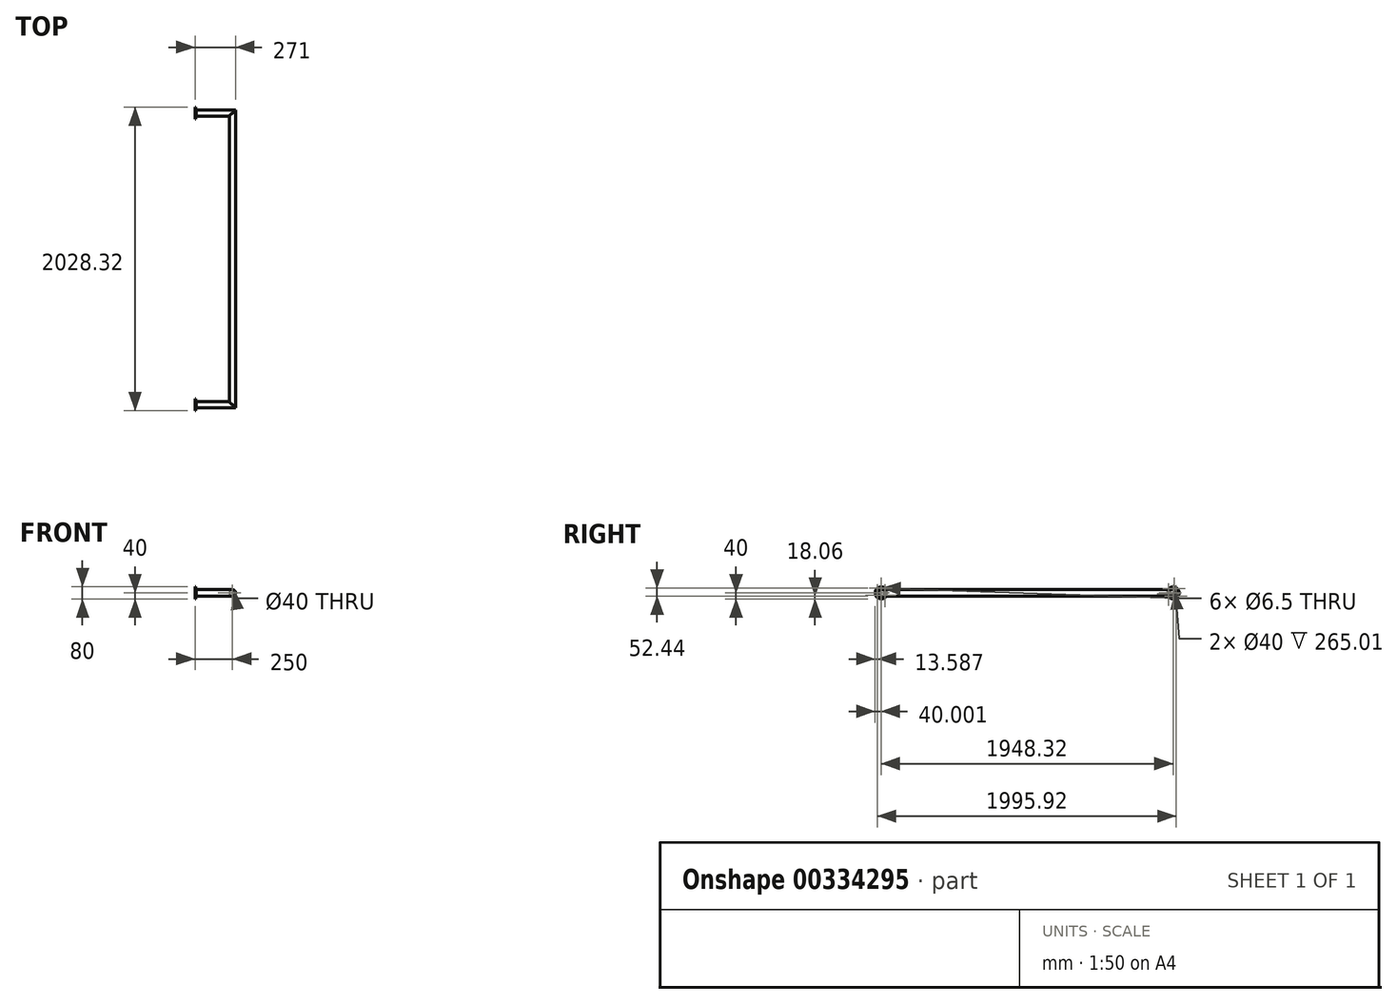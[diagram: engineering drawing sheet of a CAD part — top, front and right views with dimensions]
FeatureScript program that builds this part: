
annotation { "Feature Type Name" : "Feature", "Feature Type Description" : "" }
export const myFeature = defineFeature(function(context is Context, id is Id, definition is map)
    precondition{}
    {
        {
            var Q0;
            Q0=qCreatedBy(makeId("Right.planeOp"),FACE);
            var sketch = newSketch(context, id + "F0", { "sketchPlane" : qUnion([Q0])});
            skCircle(sketch, "E0", {"center": v(0, 0) * mm, "radius": 20 * mm});
            skCircle(sketch, "E1", {"center": v(0, 0) * mm, "radius": 21 * mm});
            skSolve(sketch);
        }
        {
            var Q0;
            Q0=qCreatedBy(makeId("Top.planeOp"),FACE);
            var sketch = newSketch(context, id + "F1", { "sketchPlane" : qUnion([Q0])});
            skLineSegment(sketch, "E2", {"start": v(0, 0) * mm, "end": v(250, 0) * mm});
            skLineSegment(sketch, "E3", {"start": v(250, 0) * mm, "end": v(250, -1948.32) * mm});
            skLineSegment(sketch, "E4", {"start": v(250, -1948.32) * mm, "end": v(0, -1948.32) * mm});
            skSolve(sketch);
        }
        {
            var Q0;
            Q0=makeQuery(id+"F0.imprint","IMPRINT",FACE,{"disambiguationData":[TD([[makeQuery(id+"F0.imprint","IMPRINT",EDGE,{"derivedFrom":sQuery(id+"F0.wireOp",EDGE,"E0")}),-1.0]])]});
            var Q1;
            Q1=sQuery(id+"F1.wireOp",EDGE,"E2");
            var Q2;
            Q2=sQuery(id+"F1.wireOp",EDGE,"E3");
            var Q3;
            Q3=sQuery(id+"F1.wireOp",EDGE,"E4");
            sweep(context, id + "F2", {"profiles" : qUnion([Q0]), "path" : qUnion([Q1, Q2, Q3])});
        }
        {
            var Q0;
            Q0=makeQuery(id+"F2.opSweep","CAP_FACE",FACE,{"disambiguationData":[OSD([sQuery(id+"F0.wireOp",EDGE,"E0"),sQuery(id+"F0.wireOp",EDGE,"E1"),sQuery(id+"F1.wireOp",VERTEX,"E4.end")])],"isStart":false});
            var sketch = newSketch(context, id + "F3", { "sketchPlane" : qUnion([Q0])});
            skCircle(sketch, "E5", {"center": v(1948.32, 0) * mm, "radius": 40 * mm});
            skLineSegment(sketch, "E6", {"start": v(1948.32, 40) * mm, "end": v(1948.32, -40) * mm, "construction": true});
            skPoint(sketch, "E7", {"position": v(1948.32, 21) * mm});
            skPoint(sketch, "E8", {"position": v(1948.32, -21) * mm});
            skLineSegment(sketch, "E9", {"start": v(2096.44, 30.5) * mm, "end": v(2107.58, 30.5) * mm, "construction": true});
            skLineSegment(sketch, "E10", {"start": v(2092.64, -30.5) * mm, "end": v(2107.79, -30.5) * mm, "construction": true});
            skPoint(sketch, "E11", {"position": v(1948.32, 30.5) * mm});
            skPoint(sketch, "E12", {"position": v(1948.32, -30.5) * mm});
            skCircle(sketch, "E13", {"center": v(1948.32, -30.5) * mm, "radius": 3.25 * mm, "construction": true});
            skCircle(sketch, "E14", {"center": v(1948.32, 30.5) * mm, "radius": 3.25 * mm});
            skCircle(sketch, "E15", {"center": v(0, 0) * mm, "radius": 40 * mm});
            skLineSegment(sketch, "E16", {"start": v(0, 40) * mm, "end": v(0, -40) * mm, "construction": true});
            skLineSegment(sketch, "E17", {"start": v(-15.2, 53.03) * mm, "end": v(15.2, -53.03) * mm, "construction": true});
            skPoint(sketch, "E18", {"position": v(-11.03, 38.45) * mm});
            skPoint(sketch, "E19", {"position": v(-3.3, 53.66) * mm});
            skPoint(sketch, "E20", {"position": v(-5.79, 20.19) * mm});
            skLineSegment(sketch, "E21", {"start": v(-8.4, 29.32) * mm, "end": v(-16.49, 27) * mm, "construction": true});
            skPoint(sketch, "E22", {"position": v(11.03, -38.45) * mm});
            skPoint(sketch, "E23", {"position": v(5.79, -20.19) * mm});
            skLineSegment(sketch, "E24", {"start": v(8.4, -29.32) * mm, "end": v(19.04, -26.27) * mm, "construction": true});
            skCircle(sketch, "E25", {"center": v(8.4, -29.32) * mm, "radius": 3.25 * mm, "construction": true});
            skCircle(sketch, "E26", {"center": v(-8.4, 29.32) * mm, "radius": 3.25 * mm});
            skCircle(sketch, "E27.1.0", {"center": v(-21.19, -21.94) * mm, "radius": 3.25 * mm});
            skCircle(sketch, "E27.2.0", {"center": v(29.6, -7.38) * mm, "radius": 3.25 * mm});
            skCircle(sketch, "E28.1.1", {"center": v(1921.9, -15.25) * mm, "radius": 3.25 * mm});
            skCircle(sketch, "E28.2.1", {"center": v(1974.73, -15.25) * mm, "radius": 3.25 * mm});
            skCircle(sketch, "E29", {"center": v(0, 0) * mm, "radius": 30.5 * mm, "construction": true});
            skLineSegment(sketch, "E30", {"start": v(0, 0) * mm, "end": v(29.6, -7.38) * mm, "construction": true});
            skLineSegment(sketch, "E31", {"start": v(0, 0) * mm, "end": v(-21.19, -21.94) * mm, "construction": true});
            skSolve(sketch);
        }
        {
            var Q0;
            Q0=qSketchRegion(id+"F3",true);
            extrude(context, id + "F4", {"entities" : qUnion([Q0]), "operationType" : NewBodyOperationType.ADD, "oppositeDirection" : true, "depth" : 5 * mm});
        }
        {
            var Q0;
            Q0=makeQuery(id+"F4.opExtrude","CAP_EDGE",EDGE,{"disambiguationData":[OSD([sQuery(id+"F3.wireOp",EDGE,"E26")])],"isStart":false});
            var Q1;
            Q1=makeQuery(id+"F4.opExtrude","CAP_EDGE",EDGE,{"disambiguationData":[OSD([sQuery(id+"F3.wireOp",EDGE,"E27.2.0")])],"isStart":false});
            var Q2;
            Q2=makeQuery(id+"F4.opExtrude","CAP_EDGE",EDGE,{"disambiguationData":[OSD([sQuery(id+"F3.wireOp",EDGE,"E27.1.0")])],"isStart":false});
            var Q3;
            Q3=makeQuery(id+"F4.opExtrude","CAP_EDGE",EDGE,{"disambiguationData":[OSD([sQuery(id+"F3.wireOp",EDGE,"E14")])],"isStart":false});
            var Q4;
            Q4=makeQuery(id+"F4.opExtrude","CAP_EDGE",EDGE,{"disambiguationData":[OSD([sQuery(id+"F3.wireOp",EDGE,"E28.2.1")])],"isStart":false});
            var Q5;
            Q5=makeQuery(id+"F4.opExtrude","CAP_EDGE",EDGE,{"disambiguationData":[OSD([sQuery(id+"F3.wireOp",EDGE,"E28.1.1")])],"isStart":false});
            chamfer(context, id + "F5", {"entities" : qUnion([Q0, Q1, Q2, Q3, Q4, Q5]), "width" : 2 * mm, "tangentPropagation" : true});
        }
        {
            var Q0;
            Q0=makeQuery(id+"F4.boolean.opBoolean","INTERSECT",EDGE,{"derivedFrom":[makeQuery(id+"F2.opSweep","SWEPT_FACE",FACE,{"disambiguationData":[OSD([sQuery(id+"F0.wireOp",EDGE,"E1"),sQuery(id+"F1.wireOp",EDGE,"E2")])]}),makeQuery(id+"F4.opExtrude","CAP_FACE",FACE,{"disambiguationData":[OSD([sQuery(id+"F3.wireOp",EDGE,"E15"),sQuery(id+"F3.wireOp",EDGE,"E26"),sQuery(id+"F3.wireOp",EDGE,"E27.1.0"),sQuery(id+"F3.wireOp",EDGE,"E27.2.0")])],"isStart":false})]});
            var Q1;
            Q1=makeQuery(id+"F4.boolean.opBoolean","INTERSECT",EDGE,{"derivedFrom":[makeQuery(id+"F2.opSweep","SWEPT_FACE",FACE,{"disambiguationData":[OSD([sQuery(id+"F0.wireOp",EDGE,"E1"),sQuery(id+"F1.wireOp",EDGE,"E4")])]}),makeQuery(id+"F4.opExtrude","CAP_FACE",FACE,{"disambiguationData":[OSD([sQuery(id+"F3.wireOp",EDGE,"E5"),sQuery(id+"F3.wireOp",EDGE,"E14"),sQuery(id+"F3.wireOp",EDGE,"E28.1.1"),sQuery(id+"F3.wireOp",EDGE,"E28.2.1")])],"isStart":false})]});
            chamfer(context, id + "F6", {"entities" : qUnion([Q0, Q1]), "width" : 3 * mm, "tangentPropagation" : true});
        }
    });
